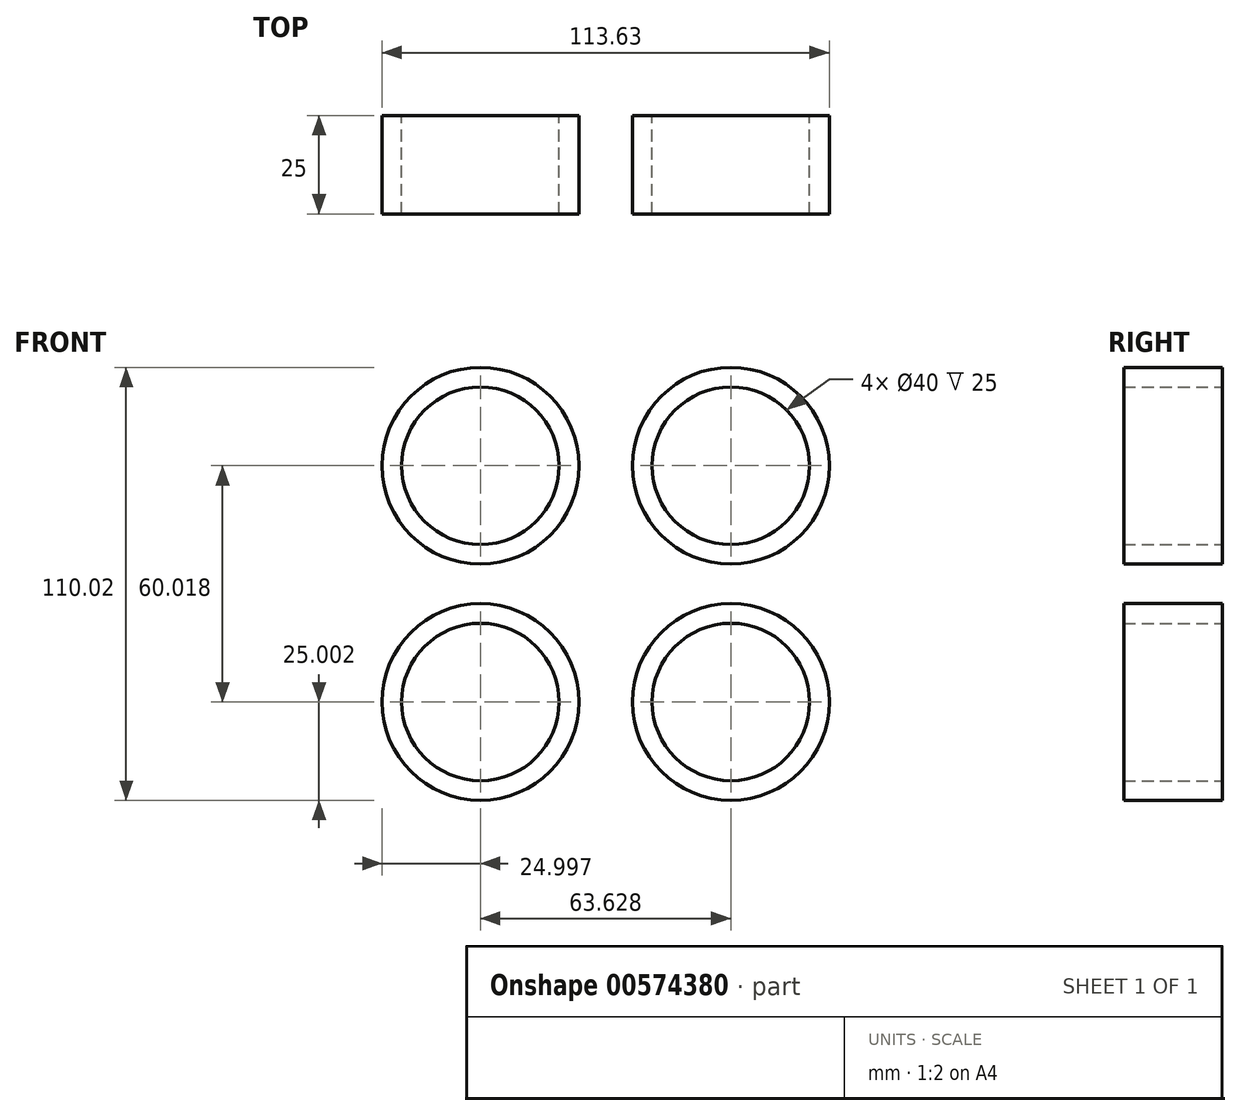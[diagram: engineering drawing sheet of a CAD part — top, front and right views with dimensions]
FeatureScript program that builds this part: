
annotation { "Feature Type Name" : "Feature", "Feature Type Description" : "" }
export const myFeature = defineFeature(function(context is Context, id is Id, definition is map)
    precondition{}
    {
        {
            var Q0;
            Q0=qCreatedBy(makeId("Front.planeOp"),FACE);
            var sketch = newSketch(context, id + "F0", { "sketchPlane" : qUnion([Q0])});
            skLineSegment(sketch, "E0.bottom", {"start": v(-32.04, 29.78) * mm, "end": v(31.59, 29.78) * mm, "construction": true});
            skLineSegment(sketch, "E0.top", {"start": v(-32.04, -30.24) * mm, "end": v(31.59, -30.24) * mm, "construction": true});
            skLineSegment(sketch, "E0.left", {"start": v(-32.04, 29.78) * mm, "end": v(-32.04, -30.24) * mm, "construction": true});
            skLineSegment(sketch, "E0.right", {"start": v(31.59, 29.78) * mm, "end": v(31.59, -30.24) * mm, "construction": true});
            skCircle(sketch, "E1", {"center": v(-32.04, 29.78) * mm, "radius": 25 * mm});
            skCircle(sketch, "E2", {"center": v(-32.04, 29.78) * mm, "radius": 20 * mm});
            skCircle(sketch, "E3", {"center": v(31.59, 29.78) * mm, "radius": 25 * mm});
            skCircle(sketch, "E4", {"center": v(31.59, 29.78) * mm, "radius": 20 * mm});
            skCircle(sketch, "E5", {"center": v(-32.04, -30.24) * mm, "radius": 25 * mm});
            skCircle(sketch, "E6", {"center": v(-32.04, -30.24) * mm, "radius": 20 * mm});
            skCircle(sketch, "E7", {"center": v(31.59, -30.24) * mm, "radius": 25 * mm});
            skCircle(sketch, "E8", {"center": v(31.59, -30.24) * mm, "radius": 20 * mm});
            skSolve(sketch);
        }
        {
            var Q0;
            Q0=makeQuery(id+"F0.imprint","IMPRINT",FACE,{"disambiguationData":[TD([[makeQuery(id+"F0.imprint","IMPRINT",EDGE,{"derivedFrom":sQuery(id+"F0.wireOp",EDGE,"E1")}),1.0]])]});
            var Q1;
            Q1=makeQuery(id+"F0.imprint","IMPRINT",FACE,{"disambiguationData":[TD([[makeQuery(id+"F0.imprint","IMPRINT",EDGE,{"derivedFrom":sQuery(id+"F0.wireOp",EDGE,"E3")}),1.0]])]});
            var Q2;
            Q2=makeQuery(id+"F0.imprint","IMPRINT",FACE,{"disambiguationData":[TD([[makeQuery(id+"F0.imprint","IMPRINT",EDGE,{"derivedFrom":sQuery(id+"F0.wireOp",EDGE,"E7")}),1.0]])]});
            var Q3;
            Q3=makeQuery(id+"F0.imprint","IMPRINT",FACE,{"disambiguationData":[TD([[makeQuery(id+"F0.imprint","IMPRINT",EDGE,{"derivedFrom":sQuery(id+"F0.wireOp",EDGE,"E5")}),1.0]])]});
            extrude(context, id + "F1", {"entities" : qUnion([Q0, Q1, Q2, Q3]), "endBound" : BoundingType.SYMMETRIC, "depth" : 25 * mm, "offsetDistance" : 25 * mm});
        }
    });
